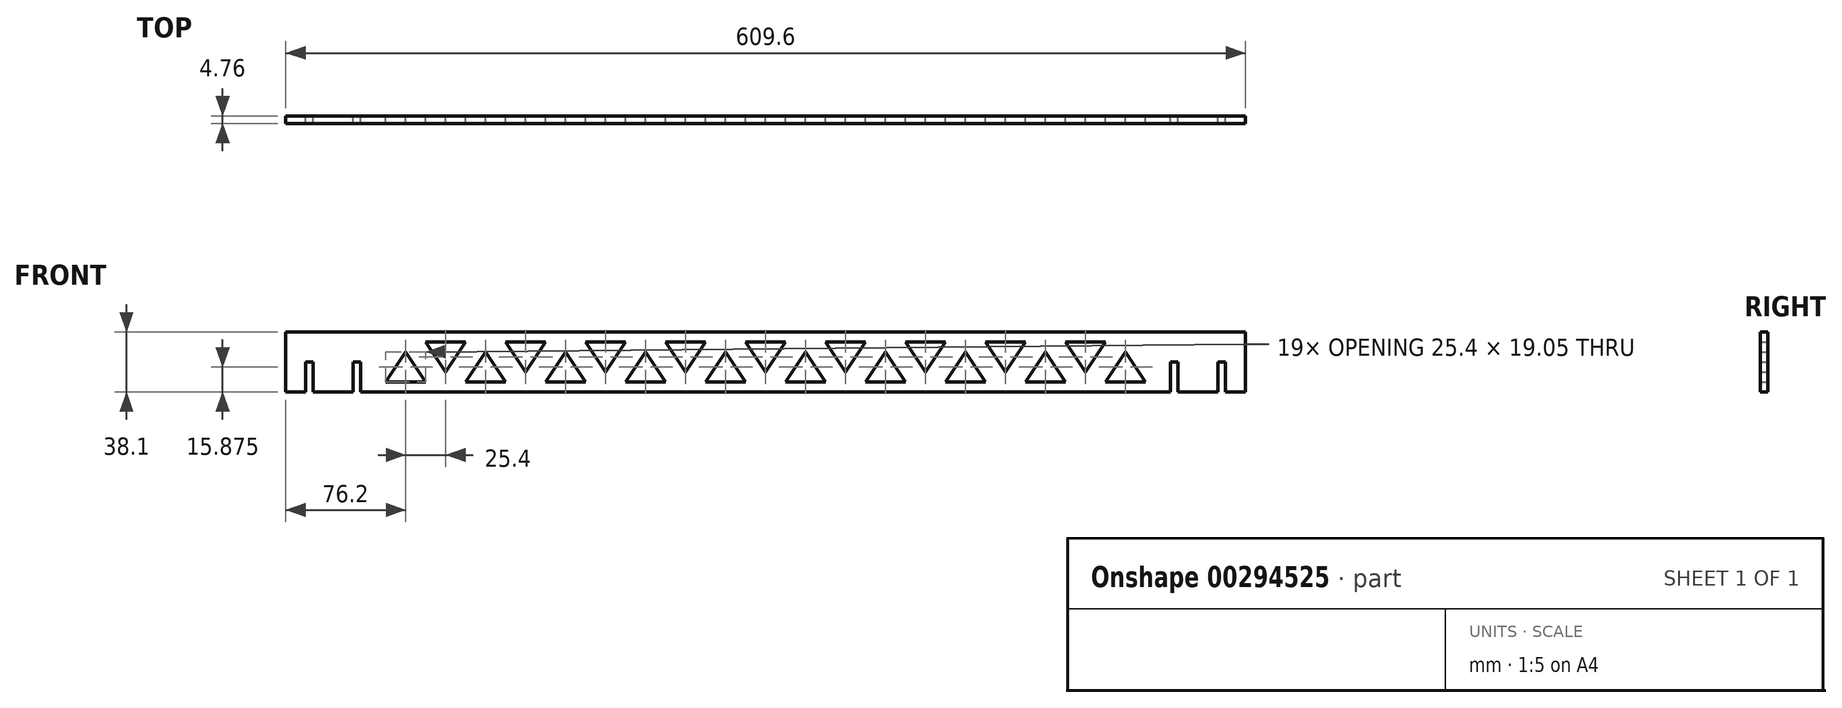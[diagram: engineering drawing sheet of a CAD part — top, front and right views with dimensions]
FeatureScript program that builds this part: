
annotation { "Feature Type Name" : "Feature", "Feature Type Description" : "" }
export const myFeature = defineFeature(function(context is Context, id is Id, definition is map)
    precondition{}
    {
        {
            var Q0;
            Q0=qCreatedBy(makeId("Front.planeOp"),FACE);
            var sketch = newSketch(context, id + "F0", { "sketchPlane" : qUnion([Q0])});
            skLineSegment(sketch, "E0.bottom", {"start": v(0, 0) * mm, "end": v(12.7, 0) * mm});
            skLineSegment(sketch, "E0.top", {"start": v(0, 38.1) * mm, "end": v(609.6, 38.1) * mm});
            skLineSegment(sketch, "E0.left", {"start": v(0, 0) * mm, "end": v(0, 38.1) * mm});
            skLineSegment(sketch, "E0.right", {"start": v(609.6, 0) * mm, "end": v(609.6, 38.1) * mm});
            skLineSegment(sketch, "E1.top", {"start": v(12.7, 19.05) * mm, "end": v(17.46, 19.05) * mm});
            skLineSegment(sketch, "E1.left", {"start": v(12.7, 0) * mm, "end": v(12.7, 19.05) * mm});
            skLineSegment(sketch, "E1.right", {"start": v(17.46, 0) * mm, "end": v(17.46, 19.05) * mm});
            skLineSegment(sketch, "E2.top", {"start": v(42.86, 19.05) * mm, "end": v(47.62, 19.05) * mm});
            skLineSegment(sketch, "E2.left", {"start": v(42.86, 0) * mm, "end": v(42.86, 19.05) * mm});
            skLineSegment(sketch, "E2.right", {"start": v(47.62, 0) * mm, "end": v(47.62, 19.05) * mm});
            skLineSegment(sketch, "E3.trimOffspring", {"start": v(304.8, 0) * mm, "end": v(561.98, 0) * mm});
            skLineSegment(sketch, "E4.trimOffspring", {"start": v(17.46, 0) * mm, "end": v(42.86, 0) * mm});
            skLineSegment(sketch, "E5.MirrorCS", {"start": v(304.8, 0) * mm, "end": v(47.62, 0) * mm});
            skPoint(sketch, "E6.orphan", {"position": v(609.6, 38.1) * mm});
            skPoint(sketch, "E7.MirrorCS.end.orphan", {"position": v(0, 38.1) * mm});
            skLineSegment(sketch, "E8.trimOffspring", {"start": v(12.7, 0) * mm, "end": v(0, 0) * mm});
            skLineSegment(sketch, "E9.trimOffspring", {"start": v(42.86, 0) * mm, "end": v(17.46, 0) * mm});
            skLineSegment(sketch, "E10.bottom", {"start": v(63.5, 31.75) * mm, "end": v(114.3, 31.75) * mm, "construction": true});
            skLineSegment(sketch, "E10.top", {"start": v(63.5, 6.35) * mm, "end": v(114.3, 6.35) * mm, "construction": true});
            skLineSegment(sketch, "E10.left", {"start": v(63.5, 31.75) * mm, "end": v(63.5, 6.35) * mm, "construction": true});
            skLineSegment(sketch, "E10.right", {"start": v(114.3, 31.75) * mm, "end": v(114.3, 6.35) * mm, "construction": true});
            skLineSegment(sketch, "E11", {"start": v(88.9, 31.75) * mm, "end": v(101.6, 12.7) * mm});
            skPoint(sketch, "E11.endSnap0", {"position": v(114.3, 19.05) * mm});
            skLineSegment(sketch, "E12", {"start": v(101.6, 12.7) * mm, "end": v(114.3, 31.75) * mm});
            skLineSegment(sketch, "E13", {"start": v(63.5, 6.35) * mm, "end": v(76.2, 25.4) * mm});
            skLineSegment(sketch, "E14", {"start": v(76.2, 25.4) * mm, "end": v(88.9, 6.35) * mm});
            skLineSegment(sketch, "E15", {"start": v(63.5, 6.35) * mm, "end": v(88.9, 6.35) * mm});
            skLineSegment(sketch, "E16", {"start": v(114.3, 31.75) * mm, "end": v(88.9, 31.75) * mm});
            skLineSegment(sketch, "E17.1.0.0", {"start": v(165.1, 31.75) * mm, "end": v(165.1, 6.35) * mm, "construction": true});
            skLineSegment(sketch, "E17.1.0.1", {"start": v(127, 25.4) * mm, "end": v(139.7, 6.35) * mm});
            skPoint(sketch, "E17.1.0.2", {"position": v(165.1, 19.05) * mm});
            skLineSegment(sketch, "E17.1.0.3", {"start": v(152.4, 12.7) * mm, "end": v(165.1, 31.75) * mm});
            skLineSegment(sketch, "E17.1.0.4", {"start": v(139.7, 31.75) * mm, "end": v(152.4, 12.7) * mm});
            skLineSegment(sketch, "E17.1.0.5", {"start": v(114.3, 6.35) * mm, "end": v(127, 25.4) * mm});
            skLineSegment(sketch, "E17.1.0.6", {"start": v(114.3, 6.35) * mm, "end": v(165.1, 6.35) * mm, "construction": true});
            skLineSegment(sketch, "E17.1.0.8", {"start": v(114.3, 31.75) * mm, "end": v(165.1, 31.75) * mm, "construction": true});
            skLineSegment(sketch, "E17.1.0.9", {"start": v(114.3, 6.35) * mm, "end": v(139.7, 6.35) * mm});
            skLineSegment(sketch, "E17.1.0.10", {"start": v(165.1, 31.75) * mm, "end": v(139.7, 31.75) * mm});
            skLineSegment(sketch, "E18.0.2.0", {"start": v(215.9, 31.75) * mm, "end": v(215.9, 6.35) * mm, "construction": true});
            skLineSegment(sketch, "E18.3.2.0", {"start": v(177.8, 25.4) * mm, "end": v(190.5, 6.35) * mm});
            skPoint(sketch, "E18.6.2.0", {"position": v(215.9, 19.05) * mm});
            skLineSegment(sketch, "E18.7.2.0", {"start": v(203.2, 12.7) * mm, "end": v(215.9, 31.75) * mm});
            skLineSegment(sketch, "E18.10.2.0", {"start": v(190.5, 31.75) * mm, "end": v(203.2, 12.7) * mm});
            skLineSegment(sketch, "E18.13.2.0", {"start": v(165.1, 6.35) * mm, "end": v(177.8, 25.4) * mm});
            skLineSegment(sketch, "E18.16.2.0", {"start": v(165.1, 6.35) * mm, "end": v(215.9, 6.35) * mm, "construction": true});
            skLineSegment(sketch, "E18.22.2.0", {"start": v(165.1, 31.75) * mm, "end": v(215.9, 31.75) * mm, "construction": true});
            skLineSegment(sketch, "E18.25.2.0", {"start": v(165.1, 6.35) * mm, "end": v(190.5, 6.35) * mm});
            skLineSegment(sketch, "E18.28.2.0", {"start": v(215.9, 31.75) * mm, "end": v(190.5, 31.75) * mm});
            skLineSegment(sketch, "E19", {"start": v(304.8, 0) * mm, "end": v(304.8, 38.1) * mm, "construction": true});
            skLineSegment(sketch, "E20.0.3.0", {"start": v(266.7, 31.75) * mm, "end": v(266.7, 6.35) * mm, "construction": true});
            skLineSegment(sketch, "E20.3.3.0", {"start": v(228.6, 25.4) * mm, "end": v(241.3, 6.35) * mm});
            skPoint(sketch, "E20.6.3.0", {"position": v(266.7, 19.05) * mm});
            skLineSegment(sketch, "E20.7.3.0", {"start": v(254, 12.7) * mm, "end": v(266.7, 31.75) * mm});
            skLineSegment(sketch, "E20.10.3.0", {"start": v(241.3, 31.75) * mm, "end": v(254, 12.7) * mm});
            skLineSegment(sketch, "E20.13.3.0", {"start": v(215.9, 6.35) * mm, "end": v(228.6, 25.4) * mm});
            skLineSegment(sketch, "E20.16.3.0", {"start": v(215.9, 6.35) * mm, "end": v(266.7, 6.35) * mm, "construction": true});
            skLineSegment(sketch, "E20.22.3.0", {"start": v(215.9, 31.75) * mm, "end": v(266.7, 31.75) * mm, "construction": true});
            skLineSegment(sketch, "E20.25.3.0", {"start": v(215.9, 6.35) * mm, "end": v(241.3, 6.35) * mm});
            skLineSegment(sketch, "E20.28.3.0", {"start": v(266.7, 31.75) * mm, "end": v(241.3, 31.75) * mm});
            skLineSegment(sketch, "E21.MirrorCS", {"start": v(444.5, 31.75) * mm, "end": v(444.5, 6.35) * mm, "construction": true});
            skLineSegment(sketch, "E22.MirrorCS", {"start": v(495.3, 31.75) * mm, "end": v(495.3, 6.35) * mm, "construction": true});
            skLineSegment(sketch, "E23.MirrorCS", {"start": v(393.7, 31.75) * mm, "end": v(393.7, 6.35) * mm, "construction": true});
            skLineSegment(sketch, "E24.MirrorCS", {"start": v(546.1, 6.35) * mm, "end": v(520.7, 6.35) * mm});
            skLineSegment(sketch, "E25.MirrorCS", {"start": v(355.6, 12.7) * mm, "end": v(342.9, 31.75) * mm});
            skLineSegment(sketch, "E26.MirrorCS", {"start": v(444.5, 6.35) * mm, "end": v(431.8, 25.4) * mm});
            skLineSegment(sketch, "E27.MirrorCS", {"start": v(546.1, 6.35) * mm, "end": v(495.3, 6.35) * mm, "construction": true});
            skLineSegment(sketch, "E28.MirrorCS", {"start": v(342.9, 31.75) * mm, "end": v(368.3, 31.75) * mm});
            skLineSegment(sketch, "E29.MirrorCS", {"start": v(393.7, 6.35) * mm, "end": v(381, 25.4) * mm});
            skLineSegment(sketch, "E30.MirrorCS", {"start": v(457.2, 12.7) * mm, "end": v(444.5, 31.75) * mm});
            skLineSegment(sketch, "E31.MirrorCS", {"start": v(393.7, 6.35) * mm, "end": v(368.3, 6.35) * mm});
            skLineSegment(sketch, "E32.MirrorCS", {"start": v(393.7, 31.75) * mm, "end": v(419.1, 31.75) * mm});
            skLineSegment(sketch, "E33.MirrorCS", {"start": v(406.4, 12.7) * mm, "end": v(393.7, 31.75) * mm});
            skLineSegment(sketch, "E34.MirrorCS", {"start": v(495.3, 6.35) * mm, "end": v(469.9, 6.35) * mm});
            skLineSegment(sketch, "E35.MirrorCS", {"start": v(444.5, 6.35) * mm, "end": v(419.1, 6.35) * mm});
            skLineSegment(sketch, "E36.MirrorCS", {"start": v(495.3, 31.75) * mm, "end": v(520.7, 31.75) * mm});
            skLineSegment(sketch, "E37.MirrorCS", {"start": v(508, 12.7) * mm, "end": v(495.3, 31.75) * mm});
            skLineSegment(sketch, "E38.MirrorCS", {"start": v(444.5, 31.75) * mm, "end": v(469.9, 31.75) * mm});
            skLineSegment(sketch, "E39.MirrorCS", {"start": v(419.1, 31.75) * mm, "end": v(406.4, 12.7) * mm});
            skLineSegment(sketch, "E40.MirrorCS", {"start": v(495.3, 6.35) * mm, "end": v(482.6, 25.4) * mm});
            skLineSegment(sketch, "E41.MirrorCS", {"start": v(546.1, 31.75) * mm, "end": v(546.1, 6.35) * mm, "construction": true});
            skPoint(sketch, "E42.MirrorP", {"position": v(444.5, 19.05) * mm});
            skLineSegment(sketch, "E43.MirrorCS", {"start": v(482.6, 25.4) * mm, "end": v(469.9, 6.35) * mm});
            skLineSegment(sketch, "E44.MirrorCS", {"start": v(469.9, 31.75) * mm, "end": v(457.2, 12.7) * mm});
            skLineSegment(sketch, "E45.MirrorCS", {"start": v(495.3, 31.75) * mm, "end": v(444.5, 31.75) * mm, "construction": true});
            skLineSegment(sketch, "E46.MirrorCS", {"start": v(381, 25.4) * mm, "end": v(368.3, 6.35) * mm});
            skLineSegment(sketch, "E47.MirrorCS", {"start": v(533.4, 25.4) * mm, "end": v(520.7, 6.35) * mm});
            skPoint(sketch, "E48.MirrorP", {"position": v(342.9, 19.05) * mm});
            skPoint(sketch, "E49.MirrorP", {"position": v(393.7, 19.05) * mm});
            skLineSegment(sketch, "E50.MirrorCS", {"start": v(393.7, 31.75) * mm, "end": v(342.9, 31.75) * mm, "construction": true});
            skPoint(sketch, "E51.MirrorP", {"position": v(495.3, 19.05) * mm});
            skLineSegment(sketch, "E52.MirrorCS", {"start": v(444.5, 31.75) * mm, "end": v(393.7, 31.75) * mm, "construction": true});
            skLineSegment(sketch, "E53.MirrorCS", {"start": v(520.7, 31.75) * mm, "end": v(508, 12.7) * mm});
            skLineSegment(sketch, "E54.MirrorCS", {"start": v(368.3, 31.75) * mm, "end": v(355.6, 12.7) * mm});
            skLineSegment(sketch, "E55.MirrorCS", {"start": v(393.7, 6.35) * mm, "end": v(342.9, 6.35) * mm, "construction": true});
            skLineSegment(sketch, "E56.MirrorCS", {"start": v(546.1, 6.35) * mm, "end": v(533.4, 25.4) * mm});
            skLineSegment(sketch, "E57.MirrorCS", {"start": v(431.8, 25.4) * mm, "end": v(419.1, 6.35) * mm});
            skLineSegment(sketch, "E58.MirrorCS", {"start": v(546.1, 31.75) * mm, "end": v(495.3, 31.75) * mm, "construction": true});
            skLineSegment(sketch, "E59.MirrorCS", {"start": v(444.5, 6.35) * mm, "end": v(393.7, 6.35) * mm, "construction": true});
            skLineSegment(sketch, "E60.MirrorCS", {"start": v(609.6, 38.1) * mm, "end": v(0, 38.1) * mm});
            skLineSegment(sketch, "E61.MirrorCS", {"start": v(495.3, 6.35) * mm, "end": v(444.5, 6.35) * mm, "construction": true});
            skLineSegment(sketch, "E62.MirrorCS", {"start": v(596.9, 0) * mm, "end": v(609.6, 0) * mm});
            skLineSegment(sketch, "E63.MirrorCS", {"start": v(609.6, 0) * mm, "end": v(596.9, 0) * mm});
            skLineSegment(sketch, "E64.MirrorCS", {"start": v(566.74, 19.05) * mm, "end": v(561.98, 19.05) * mm});
            skLineSegment(sketch, "E65.MirrorCS", {"start": v(566.74, 0) * mm, "end": v(592.14, 0) * mm});
            skLineSegment(sketch, "E66.MirrorCS", {"start": v(596.9, 19.05) * mm, "end": v(592.14, 19.05) * mm});
            skLineSegment(sketch, "E67.MirrorCS", {"start": v(592.14, 0) * mm, "end": v(566.74, 0) * mm});
            skLineSegment(sketch, "E68.MirrorCS", {"start": v(592.14, 0) * mm, "end": v(592.14, 19.05) * mm});
            skLineSegment(sketch, "E69.MirrorCS", {"start": v(596.9, 0) * mm, "end": v(596.9, 19.05) * mm});
            skLineSegment(sketch, "E70.MirrorCS", {"start": v(561.98, 0) * mm, "end": v(561.98, 19.05) * mm});
            skLineSegment(sketch, "E71.MirrorCS", {"start": v(566.74, 0) * mm, "end": v(566.74, 19.05) * mm});
            skPoint(sketch, "E72.MirrorCS.start.orphan", {"position": v(304.8, 0) * mm});
            skLineSegment(sketch, "E73.0.4.0", {"start": v(317.5, 31.75) * mm, "end": v(317.5, 6.35) * mm, "construction": true});
            skLineSegment(sketch, "E73.3.4.0", {"start": v(279.4, 25.4) * mm, "end": v(292.1, 6.35) * mm});
            skPoint(sketch, "E73.6.4.0", {"position": v(317.5, 19.05) * mm});
            skLineSegment(sketch, "E73.7.4.0", {"start": v(304.8, 12.7) * mm, "end": v(317.5, 31.75) * mm});
            skLineSegment(sketch, "E73.10.4.0", {"start": v(292.1, 31.75) * mm, "end": v(304.8, 12.7) * mm});
            skLineSegment(sketch, "E73.13.4.0", {"start": v(266.7, 6.35) * mm, "end": v(279.4, 25.4) * mm});
            skLineSegment(sketch, "E73.16.4.0", {"start": v(266.7, 6.35) * mm, "end": v(317.5, 6.35) * mm, "construction": true});
            skLineSegment(sketch, "E73.22.4.0", {"start": v(266.7, 31.75) * mm, "end": v(317.5, 31.75) * mm, "construction": true});
            skLineSegment(sketch, "E73.25.4.0", {"start": v(266.7, 6.35) * mm, "end": v(292.1, 6.35) * mm});
            skLineSegment(sketch, "E73.28.4.0", {"start": v(317.5, 31.75) * mm, "end": v(292.1, 31.75) * mm});
            skLineSegment(sketch, "E74.MirrorCS", {"start": v(342.9, 6.35) * mm, "end": v(317.5, 6.35) * mm});
            skLineSegment(sketch, "E75.MirrorCS", {"start": v(330.2, 25.4) * mm, "end": v(317.5, 6.35) * mm});
            skLineSegment(sketch, "E76.MirrorCS", {"start": v(342.9, 6.35) * mm, "end": v(330.2, 25.4) * mm});
            skSolve(sketch);
        }
        {
            var Q0;
            Q0 = qSketchRegion(id + "F0", true);
            extrude(context, id + "F1", {"entities" : qUnion([Q0]), "depth" : 4.76 * mm});
        }
    });
